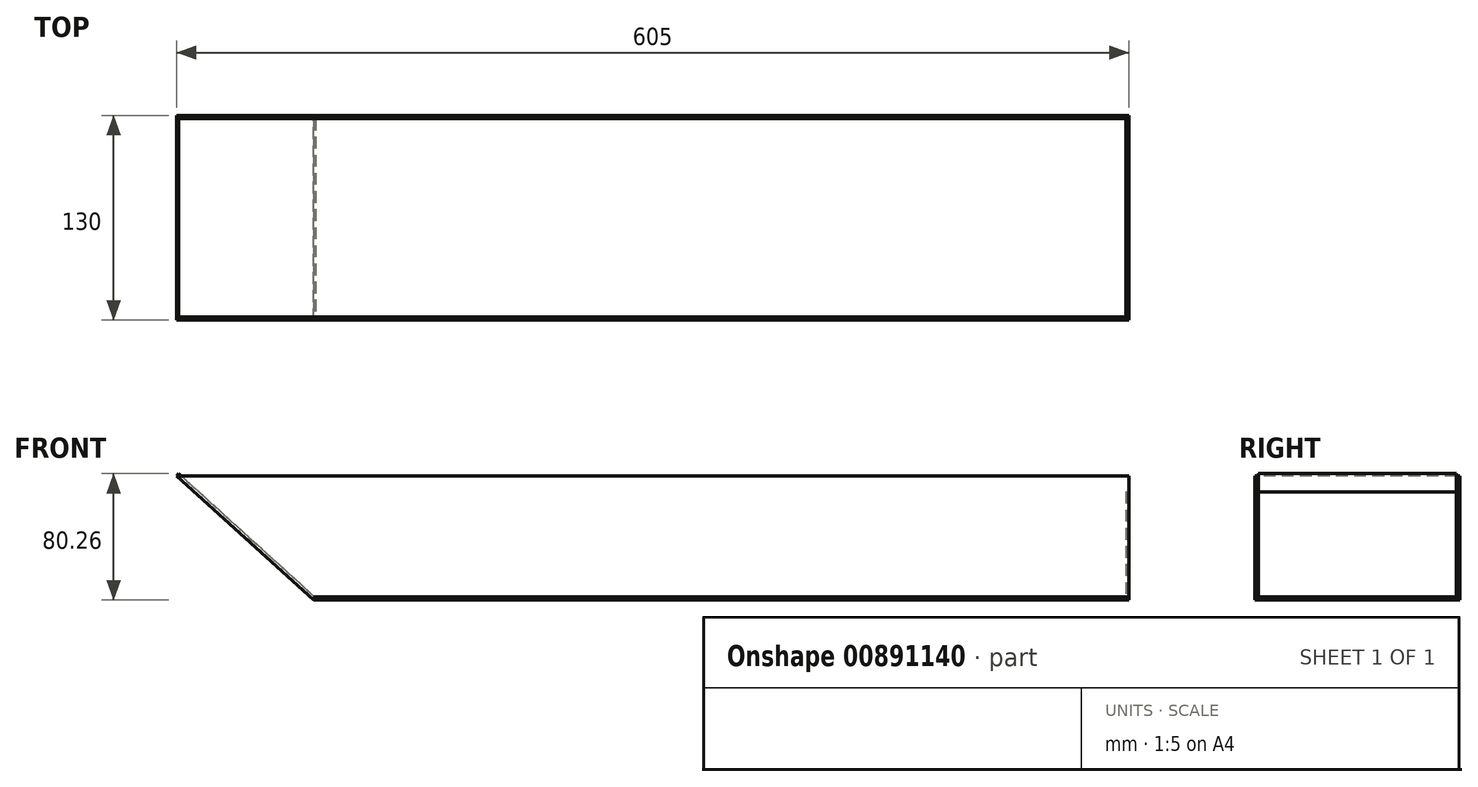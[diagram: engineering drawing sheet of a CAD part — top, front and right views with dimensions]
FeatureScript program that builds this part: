
annotation { "Feature Type Name" : "Feature", "Feature Type Description" : "" }
export const myFeature = defineFeature(function(context is Context, id is Id, definition is map)
    precondition{}
    {
        {
            var Q0;
            Q0=qCreatedBy(makeId("Front.planeOp"),FACE);
            var sketch = newSketch(context, id + "F0", { "sketchPlane" : qUnion([Q0])});
            skLineSegment(sketch, "E0.bottom", {"start": v(-259, -39.39) * mm, "end": v(259, -39.39) * mm});
            skLineSegment(sketch, "E0.right", {"start": v(259, -39.39) * mm, "end": v(259, 39.39) * mm});
            skPoint(sketch, "E0.middle", {"position": v(0, 0) * mm});
            skPoint(sketch, "E0.left.end.orphan", {"position": v(-259, 39.39) * mm});
            skLineSegment(sketch, "E1", {"start": v(259, 39.39) * mm, "end": v(-346, 39.39) * mm});
            skLineSegment(sketch, "E2", {"start": v(-259, -39.39) * mm, "end": v(-346, 39.39) * mm});
            skSolve(sketch);
        }
        {
            var Q0;
            Q0=makeQuery(id+"F0.imprint","IMPRINT",FACE,{"disambiguationData":[TD([[makeQuery(id+"F0.imprint","IMPRINT",EDGE,{"derivedFrom":sQuery(id+"F0.wireOp",EDGE,"E0.bottom")}),1.0]])]});
            cPlane(context, id + "F1", {"entities" : qUnion([Q0]), "cplaneType" : CPlaneType.OFFSET, "offset" : 65 * mm, "width" : 150 * mm, "height" : 150 * mm});
        }
        {
            var Q0;
            Q0 = qSketchRegion(id + "F0", true);
            extrude(context, id + "F2", {"entities" : qUnion([Q0]), "depth" : 2 * mm, "offsetDistance" : 25 * mm});
        }
        {
            var Q0;
            Q0=makeQuery(id+"F2.opExtrude","SWEPT_BODY",BODY,{"disambiguationData":[OSD([sQuery(id+"F0.wireOp",EDGE,"E0.bottom"),sQuery(id+"F0.wireOp",EDGE,"E0.right"),sQuery(id+"F0.wireOp",EDGE,"E1"),sQuery(id+"F0.wireOp",EDGE,"E2")])]});
            var Q1;
            Q1=qCreatedBy(id+"F1.planeOp",FACE);
            mirror(context, id + "F3", {"entities" : qUnion([Q0]), "mirrorPlane" : qUnion([Q1])});
        }
        {
            var Q0;
            Q0=makeQuery(id+"F3.opPattern","COPY",FACE,{"derivedFrom":makeQuery(id+"F2.opExtrude","SWEPT_FACE",FACE,{"disambiguationData":[OSD([sQuery(id+"F0.wireOp",EDGE,"E0.right")])]}),"instanceName":"1"});
            var sketch = newSketch(context, id + "F4", { "sketchPlane" : qUnion([Q0])});
            skLineSegment(sketch, "E3.top", {"start": v(-128, -39.32) * mm, "end": v(0, -39.32) * mm});
            skLineSegment(sketch, "E3.left", {"start": v(-128, 39.39) * mm, "end": v(-128, -39.32) * mm});
            skLineSegment(sketch, "E3.right", {"start": v(0, 39.39) * mm, "end": v(0, -39.32) * mm});
            skLineSegment(sketch, "E4", {"start": v(0, 0) * mm, "end": v(0, 5.36) * mm, "construction": true});
            skLineSegment(sketch, "E5", {"start": v(-2, 42.72) * mm, "end": v(-2, 8.11) * mm, "construction": true});
            skLineSegment(sketch, "E6", {"start": v(-2, 8.11) * mm, "end": v(-2, -47.61) * mm, "construction": true});
            skLineSegment(sketch, "E7", {"start": v(-128, -39.39) * mm, "end": v(10, -39.39) * mm, "construction": true});
            skLineSegment(sketch, "E8.top", {"start": v(-128, -39.39) * mm, "end": v(-2, -39.39) * mm});
            skLineSegment(sketch, "E8.left", {"start": v(-128, 39.39) * mm, "end": v(-128, -39.39) * mm});
            skLineSegment(sketch, "E8.right", {"start": v(-2, 39.39) * mm, "end": v(-2, -39.39) * mm});
            skLineSegment(sketch, "E9.bottom", {"start": v(-128, 39.39) * mm, "end": v(-2, 39.39) * mm});
            skSolve(sketch);
        }
        {
            var Q0;
            Q0 = qSketchRegion(id + "F4", true);
            extrude(context, id + "F5", {"entities" : qUnion([Q0]), "operationType" : NewBodyOperationType.ADD, "oppositeDirection" : true, "depth" : 2 * mm, "offsetDistance" : 25 * mm});
        }
        {
            var Q0;
            Q0 = qSketchRegion(id + "F4", true);
            extrude(context, id + "F6", {"entities" : qUnion([Q0]), "oppositeDirection" : true, "depth" : 2 * mm, "offsetDistance" : 25 * mm});
        }
        {
            var Q0;
            Q0=makeQuery(id+"F2.opExtrude","SWEPT_FACE",FACE,{"disambiguationData":[OSD([sQuery(id+"F0.wireOp",EDGE,"E2")])]});
            var sketch = newSketch(context, id + "F7", { "sketchPlane" : qUnion([Q0])});
            skLineSegment(sketch, "E10.bottom", {"start": v(-282.92, 2) * mm, "end": v(-165.56, 2) * mm});
            skLineSegment(sketch, "E10.top", {"start": v(-282.92, 128) * mm, "end": v(-165.56, 128) * mm});
            skLineSegment(sketch, "E10.left", {"start": v(-282.92, 2) * mm, "end": v(-282.92, 128) * mm});
            skLineSegment(sketch, "E10.right", {"start": v(-165.56, 2) * mm, "end": v(-165.56, 128) * mm});
            skSolve(sketch);
        }
        {
            var Q0;
            Q0 = qSketchRegion(id + "F7", true);
            extrude(context, id + "F8", {"entities" : qUnion([Q0]), "oppositeDirection" : true, "depth" : 2 * mm, "offsetDistance" : 25 * mm});
        }
        {
            var Q0;
            Q0=makeQuery(id+"F5.boolean.opBoolean","MERGE",FACE,{"derivedFrom":[makeQuery(id+"F2.opExtrude","SWEPT_FACE",FACE,{"disambiguationData":[OSD([sQuery(id+"F0.wireOp",EDGE,"E0.bottom")])]}),makeQuery(id+"F5.opExtrude","SWEPT_FACE",FACE,{"disambiguationData":[OSD([sQuery(id+"F4.wireOp",EDGE,"E8.top")])]})]});
            var sketch = newSketch(context, id + "F9", { "sketchPlane" : qUnion([Q0])});
            skLineSegment(sketch, "E11.bottom", {"start": v(259, 0) * mm, "end": v(-259, 0) * mm});
            skLineSegment(sketch, "E11.top", {"start": v(259, 130) * mm, "end": v(-259, 130) * mm});
            skLineSegment(sketch, "E11.left", {"start": v(259, 0) * mm, "end": v(259, 130) * mm});
            skLineSegment(sketch, "E11.right", {"start": v(-259, 0) * mm, "end": v(-259, 130) * mm});
            skSolve(sketch);
        }
        {
            var Q0;
            Q0 = qSketchRegion(id + "F9", true);
            extrude(context, id + "F10", {"entities" : qUnion([Q0]), "oppositeDirection" : true, "depth" : 2 * mm, "offsetDistance" : 25 * mm});
        }
        {
            var Q0;
            Q0=makeQuery(id+"F6.opExtrude","CAP_FACE",FACE,{"disambiguationData":[OSD([sQuery(id+"F4.wireOp",EDGE,"E9.bottom"),sQuery(id+"F4.wireOp",EDGE,"E8.top"),sQuery(id+"F4.wireOp",EDGE,"E8.left"),sQuery(id+"F4.wireOp",EDGE,"E8.right")])],"isStart":true});
            var sketch = newSketch(context, id + "F11", { "sketchPlane" : qUnion([Q0])});
            skLineSegment(sketch, "E12.bottom", {"start": v(-128, 39.39) * mm, "end": v(-2, 39.39) * mm});
            skLineSegment(sketch, "E12.top", {"start": v(-128, 29.39) * mm, "end": v(-2, 29.39) * mm});
            skLineSegment(sketch, "E12.left", {"start": v(-128, 39.39) * mm, "end": v(-128, 29.39) * mm});
            skLineSegment(sketch, "E12.right", {"start": v(-2, 39.39) * mm, "end": v(-2, 29.39) * mm});
            skSolve(sketch);
        }
        {
            var Q0;
            Q0 = qSketchRegion(id + "F11", true);
            extrude(context, id + "F12", {"entities" : qUnion([Q0]), "operationType" : NewBodyOperationType.REMOVE, "oppositeDirection" : true, "depth" : 10 * mm, "offsetDistance" : 25 * mm});
        }
    });
